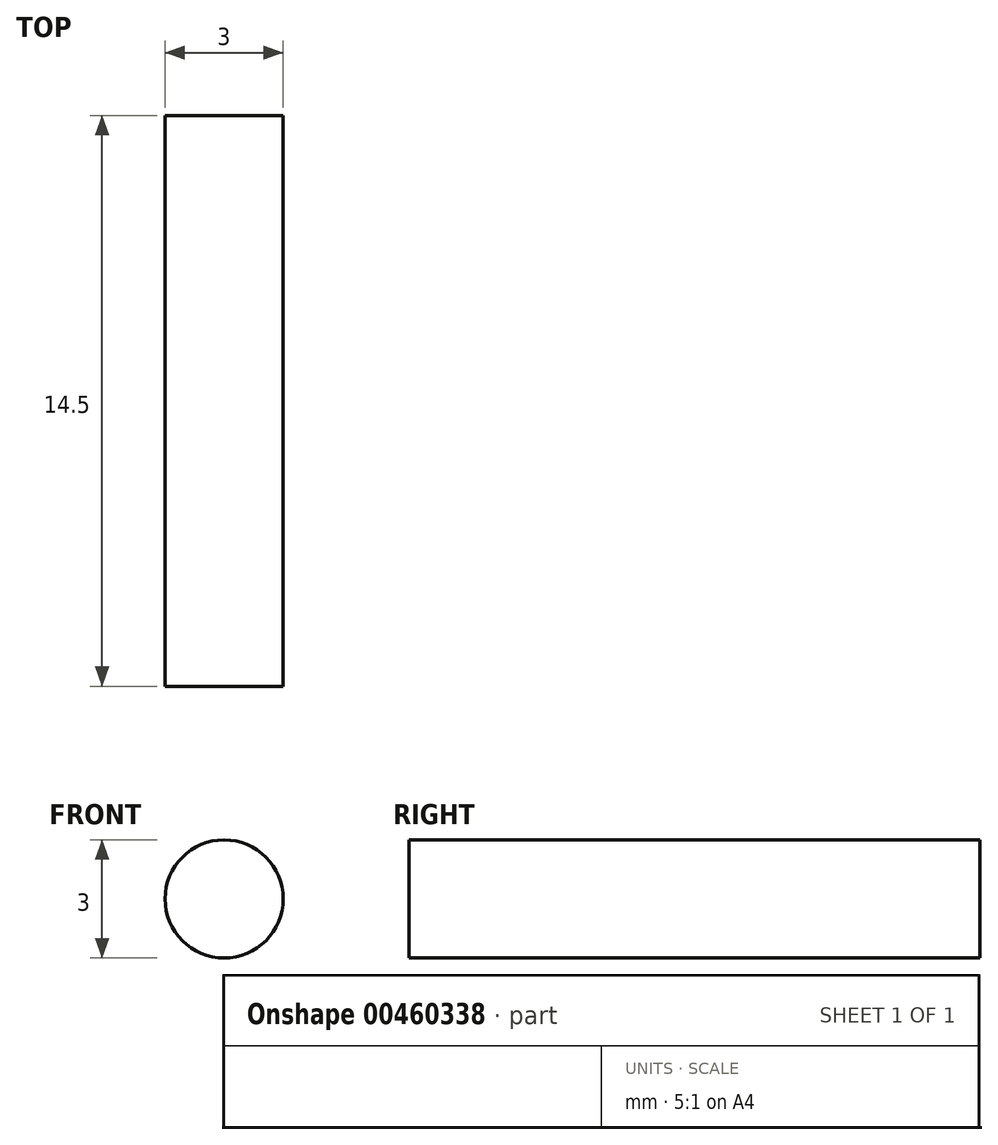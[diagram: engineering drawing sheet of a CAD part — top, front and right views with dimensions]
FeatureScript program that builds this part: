
annotation { "Feature Type Name" : "Feature", "Feature Type Description" : "" }
export const myFeature = defineFeature(function(context is Context, id is Id, definition is map)
    precondition{}
    {
        {
            var Q0;
            Q0=qCreatedBy(makeId("Front.planeOp"),FACE);
            var sketch = newSketch(context, id + "F0", { "sketchPlane" : qUnion([Q0])});
            skCircle(sketch, "E0", {"center": v(28.35, 29.18) * mm, "radius": 1.5 * mm});
            skSolve(sketch);
        }
        {
            var Q0;
            Q0=qSketchRegion(id+"F0",true);
            extrude(context, id + "F1", {"entities" : qUnion([Q0]), "depth" : 14.5 * mm});
        }
    });
